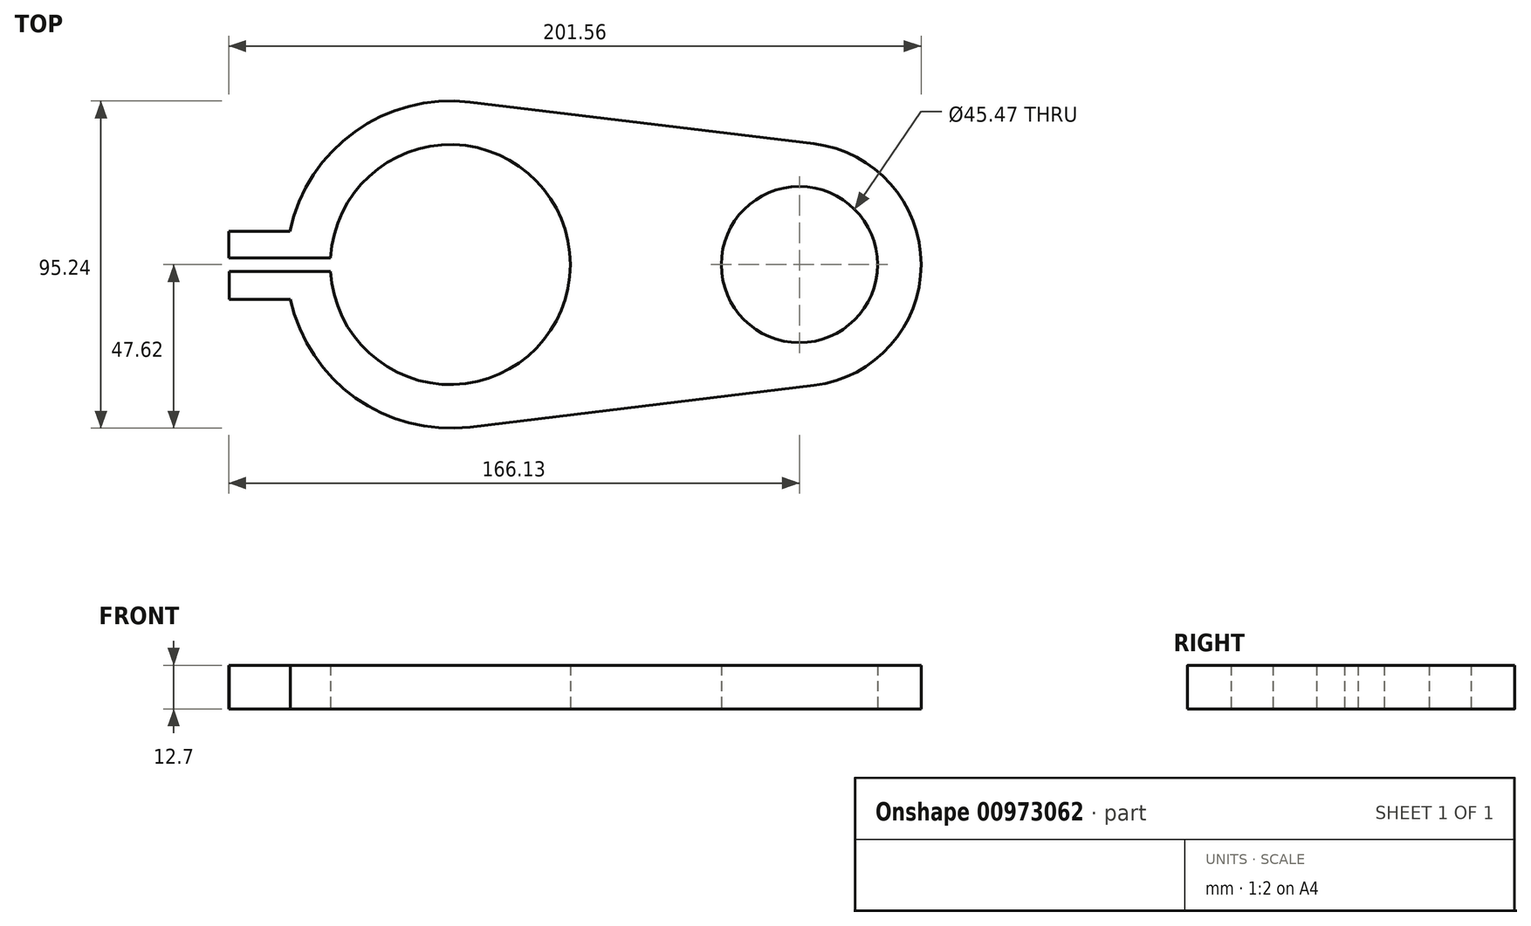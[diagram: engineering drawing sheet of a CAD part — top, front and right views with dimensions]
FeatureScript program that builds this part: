
annotation { "Feature Type Name" : "Feature", "Feature Type Description" : "" }
export const myFeature = defineFeature(function(context is Context, id is Id, definition is map)
    precondition{}
    {
        {
            var Q0;
            Q0=qCreatedBy(makeId("Top.planeOp"),FACE);
            var sketch = newSketch(context, id + "F0", { "sketchPlane" : qUnion([Q0])});
            skCircle(sketch, "E0", {"center": v(101.6, 0) * mm, "radius": 22.73 * mm});
            skLineSegment(sketch, "E1", {"start": v(5.71, 47.28) * mm, "end": v(105.85, 35.18) * mm});
            skLineSegment(sketch, "E2", {"start": v(5.71, -47.28) * mm, "end": v(105.85, -35.18) * mm});
            skArc(sketch, "E3", {"start": v(105.85, 35.18) * mm, "mid": v(137.03, 0) * mm, "end": v(105.85, -35.18) * mm});
            skPoint(sketch, "E4", {"position": v(-34.87, 2) * mm});
            skPoint(sketch, "E5", {"position": v(-47.58, 2) * mm});
            skPoint(sketch, "E6", {"position": v(-47.58, -2) * mm});
            skPoint(sketch, "E7", {"position": v(-34.87, -2) * mm});
            skLineSegment(sketch, "E8", {"start": v(-47.58, 2) * mm, "end": v(-34.87, 2) * mm});
            skLineSegment(sketch, "E9", {"start": v(-47.58, -2) * mm, "end": v(-34.87, -2) * mm});
            skLineSegment(sketch, "E10", {"start": v(-47.58, 2) * mm, "end": v(-64.53, 2) * mm});
            skLineSegment(sketch, "E11", {"start": v(-64.53, 2) * mm, "end": v(-64.53, 9.63) * mm});
            skLineSegment(sketch, "E12", {"start": v(-64.53, 9.63) * mm, "end": v(-46.64, 9.63) * mm});
            skLineSegment(sketch, "E13", {"start": v(-47.58, -2) * mm, "end": v(-64.39, -2) * mm});
            skLineSegment(sketch, "E14", {"start": v(-64.39, -2) * mm, "end": v(-64.39, -10.06) * mm});
            skLineSegment(sketch, "E15", {"start": v(-64.39, -10.06) * mm, "end": v(-46.55, -10.06) * mm});
            skArc(sketch, "E16", {"start": v(-34.87, 2) * mm, "mid": v(34.93, 0) * mm, "end": v(-34.87, -2) * mm});
            skArc(sketch, "E17", {"start": v(5.72, -47.28) * mm, "mid": v(-27.62, -38.8) * mm, "end": v(-46.55, -10.06) * mm});
            skArc(sketch, "E18", {"start": v(5.71, 47.28) * mm, "mid": v(-27.8, 38.67) * mm, "end": v(-46.64, 9.63) * mm});
            skSolve(sketch);
        }
        {
            var Q0;
            Q0 = qSketchRegion(id + "F0", true);
            extrude(context, id + "F1", {"entities" : qUnion([Q0]), "depth" : 12.7 * mm, "offsetDistance" : 25.4 * mm});
        }
    });
